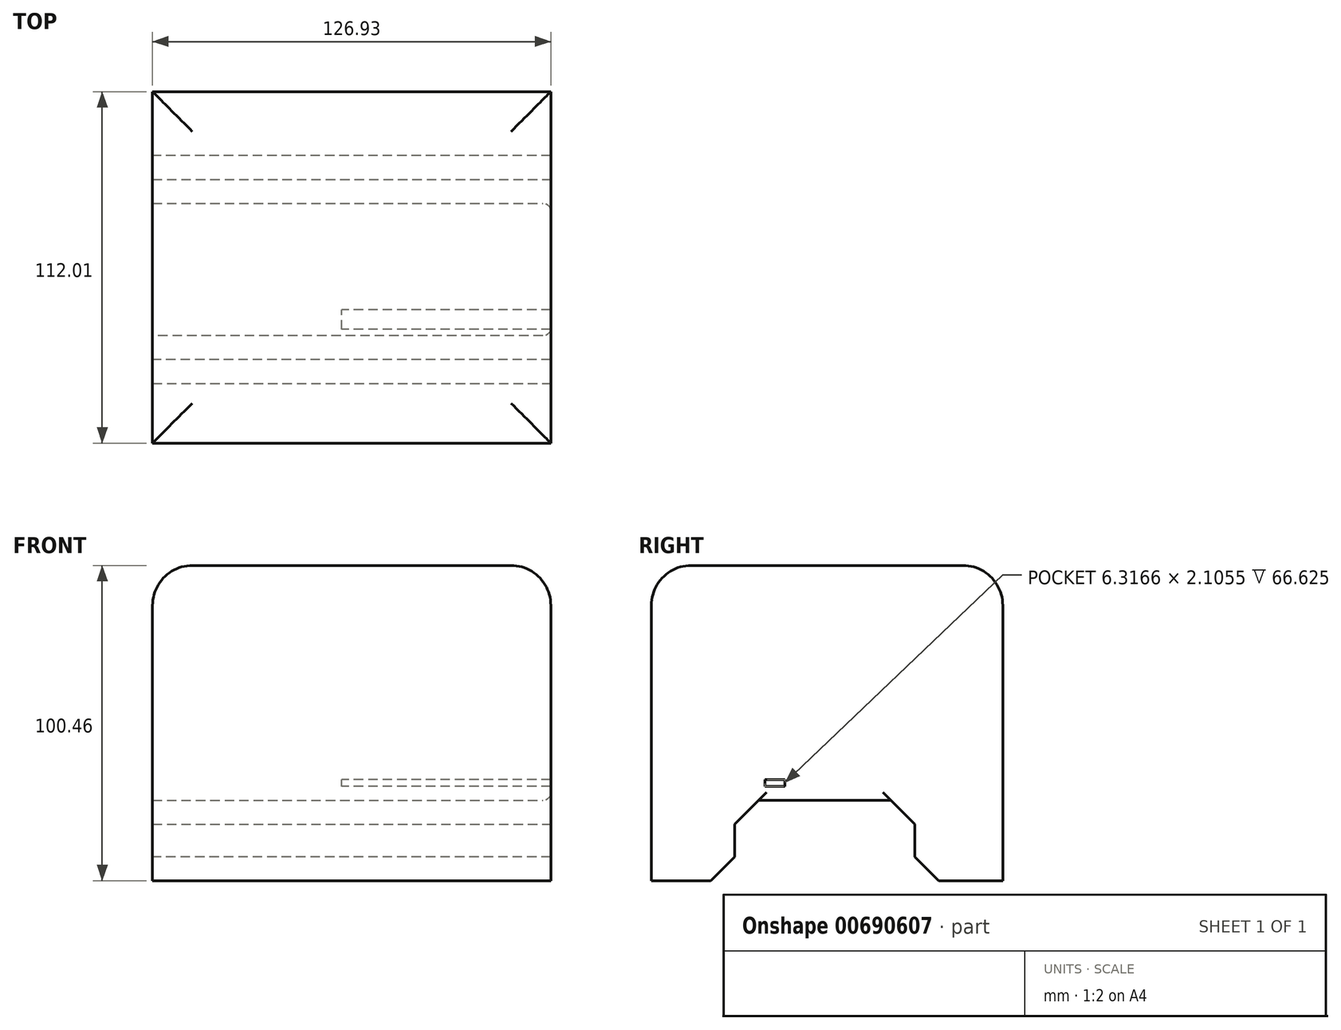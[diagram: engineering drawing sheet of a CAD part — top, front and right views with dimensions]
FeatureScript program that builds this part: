
annotation { "Feature Type Name" : "Feature", "Feature Type Description" : "" }
export const myFeature = defineFeature(function(context is Context, id is Id, definition is map)
    precondition{}
    {
        {
            var Q0;
            Q0=qCreatedBy(makeId("Front.planeOp"),FACE);
            var sketch = newSketch(context, id + "F0", { "sketchPlane" : qUnion([Q0])});
            skLineSegment(sketch, "E0.bottom", {"start": v(-60.3, 54) * mm, "end": v(66.62, 54) * mm});
            skLineSegment(sketch, "E0.top", {"start": v(-60.3, -46.47) * mm, "end": v(66.62, -46.47) * mm});
            skLineSegment(sketch, "E0.left", {"start": v(-60.3, 54) * mm, "end": v(-60.3, -46.47) * mm});
            skLineSegment(sketch, "E0.right", {"start": v(66.62, 54) * mm, "end": v(66.62, -46.47) * mm});
            skSolve(sketch);
        }
        {
            var Q0;
            Q0=makeQuery(id+"F0.imprint","IMPRINT",FACE,{"disambiguationData":[TD([[makeQuery(id+"F0.imprint","IMPRINT",EDGE,{"derivedFrom":sQuery(id+"F0.wireOp",EDGE,"E0.bottom")}),-1.0]])]});
            extrude(context, id + "F1", {"entities" : qUnion([Q0]), "depth" : 112.01 * mm, "offsetDistance" : 25.4 * mm});
        }
        {
            var Q0;
            Q0=makeQuery(id+"F1.opExtrude","CAP_EDGE",EDGE,{"disambiguationData":[OSD([sQuery(id+"F0.wireOp",EDGE,"E0.bottom")])],"isStart":false});
            var Q1;
            Q1=makeQuery(id+"F1.opExtrude","SWEPT_EDGE",EDGE,{"disambiguationData":[OSD([sQuery(id+"F0.wireOp",EDGE,"E0.bottom"),sQuery(id+"F0.wireOp",EDGE,"E0.right")])]});
            var Q2;
            Q2=makeQuery(id+"F1.opExtrude","CAP_EDGE",EDGE,{"disambiguationData":[OSD([sQuery(id+"F0.wireOp",EDGE,"E0.bottom")])],"isStart":true});
            var Q3;
            Q3=makeQuery(id+"F1.opExtrude","SWEPT_EDGE",EDGE,{"disambiguationData":[OSD([sQuery(id+"F0.wireOp",EDGE,"E0.bottom"),sQuery(id+"F0.wireOp",EDGE,"E0.left")])]});
            fillet(context, id + "F2", {"entities" : qUnion([Q0, Q1, Q2, Q3]), "radius" : 12.7 * mm, "tangentPropagation" : true, "allowEdgeOverflow" : false});
        }
        {
            var Q0;
            Q0=qCreatedBy(makeId("Right.planeOp"),FACE);
            var sketch = newSketch(context, id + "F3", { "sketchPlane" : qUnion([Q0])});
            skLineSegment(sketch, "E1.bottom", {"start": v(-85.43, -56.7) * mm, "end": v(-27.98, -56.7) * mm});
            skLineSegment(sketch, "E1.top", {"start": v(-85.43, -20.9) * mm, "end": v(-27.98, -20.9) * mm});
            skLineSegment(sketch, "E1.left", {"start": v(-85.43, -56.7) * mm, "end": v(-85.43, -20.9) * mm});
            skLineSegment(sketch, "E1.right", {"start": v(-27.98, -56.7) * mm, "end": v(-27.98, -20.9) * mm});
            skSolve(sketch);
        }
        {
            var Q0;
            Q0 = qSketchRegion(id + "F3", true);
            extrude(context, id + "F4", {"entities" : qUnion([Q0]), "depth" : 166.37 * mm, "offsetDistance" : 25.4 * mm});
        }
        {
            var Q0;
            Q0=makeQuery(id+"F4.opExtrude","CAP_FACE",FACE,{"disambiguationData":[OSD([sQuery(id+"F3.wireOp",EDGE,"E1.bottom"),sQuery(id+"F3.wireOp",EDGE,"E1.top"),sQuery(id+"F3.wireOp",EDGE,"E1.left"),sQuery(id+"F3.wireOp",EDGE,"E1.right")])],"isStart":false});
            extrude(context, id + "F5", {"entities" : qUnion([Q0]), "operationType" : NewBodyOperationType.ADD, "depth" : 99.82 * mm, "offsetDistance" : 25.4 * mm});
        }
        {
            var Q0;
            Q0=makeQuery(id+"F4.opExtrude","SWEPT_BODY",BODY,{"disambiguationData":[OSD([sQuery(id+"F3.wireOp",EDGE,"E1.bottom"),sQuery(id+"F3.wireOp",EDGE,"E1.top"),sQuery(id+"F3.wireOp",EDGE,"E1.left"),sQuery(id+"F3.wireOp",EDGE,"E1.right")])]});
            transform(context, id + "F6", {"entities" : qUnion([Q0]), "transformType" : TransformType.TRANSLATION_3D, "dx" : -151.38 * mm, "dy" : 0 * mm, "dz" : 0 * mm, "makeCopy" : false});
        }
        {
            var Q0;
            Q0=makeQuery(id+"F4.opExtrude","SWEPT_BODY",BODY,{"disambiguationData":[OSD([sQuery(id+"F3.wireOp",EDGE,"E1.bottom"),sQuery(id+"F3.wireOp",EDGE,"E1.top"),sQuery(id+"F3.wireOp",EDGE,"E1.left"),sQuery(id+"F3.wireOp",EDGE,"E1.right")])]});
            var Q1;
            Q1=makeQuery(id+"F1.opExtrude","SWEPT_BODY",BODY,{"disambiguationData":[OSD([sQuery(id+"F0.wireOp",EDGE,"E0.bottom"),sQuery(id+"F0.wireOp",EDGE,"E0.top"),sQuery(id+"F0.wireOp",EDGE,"E0.left"),sQuery(id+"F0.wireOp",EDGE,"E0.right")])]});
            booleanBodies(context, id + "F7", {"operationType" : BooleanOperationType.SUBTRACTION, "tools" : qUnion([Q0]), "targets" : qUnion([Q1])});
        }
        {
            var Q0;
            {var subQ0=sQuery(id+"F3.wireOp",EDGE,"E1.left");Q0=makeQuery(id+"F7.opBoolean","INTERSECT",EDGE,{"derivedFrom":[makeQuery(id+"F1.opExtrude","SWEPT_FACE",FACE,{"disambiguationData":[OSD([sQuery(id+"F0.wireOp",EDGE,"E0.top")])]}),makeQuery(id+"F5.boolean.opBoolean","MERGE",FACE,{"derivedFrom":[makeQuery(id+"F4.opExtrude","SWEPT_FACE",FACE,{"disambiguationData":[OSD([subQ0])]}),makeQuery(id+"F5.opExtrude","SWEPT_FACE",FACE,{"disambiguationData":[OSD([subQ0])]})]})]});}
            var Q1;
            {var subQ0=sQuery(id+"F3.wireOp",EDGE,"E1.right");Q1=makeQuery(id+"F7.opBoolean","INTERSECT",EDGE,{"derivedFrom":[makeQuery(id+"F1.opExtrude","SWEPT_FACE",FACE,{"disambiguationData":[OSD([sQuery(id+"F0.wireOp",EDGE,"E0.top")])]}),makeQuery(id+"F5.boolean.opBoolean","MERGE",FACE,{"derivedFrom":[makeQuery(id+"F4.opExtrude","SWEPT_FACE",FACE,{"disambiguationData":[OSD([subQ0])]}),makeQuery(id+"F5.opExtrude","SWEPT_FACE",FACE,{"disambiguationData":[OSD([subQ0])]})]})]});}
            var Q2;
            {var subQ0=sQuery(id+"F3.wireOp",EDGE,"E1.right");var subQ1=sQuery(id+"F3.wireOp",EDGE,"E1.top");Q2=makeQuery(id+"F7.opBoolean","COPY",EDGE,{"derivedFrom":makeQuery(id+"F5.boolean.opBoolean","MERGE",EDGE,{"derivedFrom":[makeQuery(id+"F4.opExtrude","SWEPT_EDGE",EDGE,{"disambiguationData":[OSD([subQ1,subQ0])]}),makeQuery(id+"F5.opExtrude","SWEPT_EDGE",EDGE,{"disambiguationData":[OSD([subQ1,subQ0])]})]})});}
            var Q3;
            {var subQ0=sQuery(id+"F3.wireOp",EDGE,"E1.left");var subQ1=sQuery(id+"F3.wireOp",EDGE,"E1.top");Q3=makeQuery(id+"F7.opBoolean","COPY",EDGE,{"derivedFrom":makeQuery(id+"F5.boolean.opBoolean","MERGE",EDGE,{"derivedFrom":[makeQuery(id+"F4.opExtrude","SWEPT_EDGE",EDGE,{"disambiguationData":[OSD([subQ1,subQ0])]}),makeQuery(id+"F5.opExtrude","SWEPT_EDGE",EDGE,{"disambiguationData":[OSD([subQ1,subQ0])]})]})});}
            chamfer(context, id + "F8", {"entities" : qUnion([Q0, Q1, Q2, Q3]), "width" : 7.62 * mm, "tangentPropagation" : true});
        }
        {
            var Q0;
            Q0=qCreatedBy(makeId("Right.planeOp"),FACE);
            var sketch = newSketch(context, id + "F9", { "sketchPlane" : qUnion([Q0])});
            skLineSegment(sketch, "E2.bottom", {"start": v(-75.8, -16.4) * mm, "end": v(-69.5, -16.4) * mm});
            skLineSegment(sketch, "E2.top", {"start": v(-75.8, -14.29) * mm, "end": v(-69.5, -14.29) * mm});
            skLineSegment(sketch, "E2.left", {"start": v(-75.8, -16.4) * mm, "end": v(-75.8, -14.29) * mm});
            skLineSegment(sketch, "E2.right", {"start": v(-69.5, -16.4) * mm, "end": v(-69.5, -14.29) * mm});
            skSolve(sketch);
        }
        {
            var Q0;
            Q0 = qSketchRegion(id + "F9", true);
            extrude(context, id + "F10", {"entities" : qUnion([Q0]), "operationType" : NewBodyOperationType.REMOVE, "depth" : 148.84 * mm, "offsetDistance" : 25.4 * mm});
        }
        {
            var Q0;
            {var subQ0=sQuery(id+"F3.wireOp",EDGE,"E1.top");Q0=makeQuery(id+"F7.opBoolean","INTERSECT",EDGE,{"derivedFrom":[makeQuery(id+"F1.opExtrude","SWEPT_FACE",FACE,{"disambiguationData":[OSD([sQuery(id+"F0.wireOp",EDGE,"E0.right")])]}),makeQuery(id+"F5.boolean.opBoolean","MERGE",FACE,{"derivedFrom":[makeQuery(id+"F4.opExtrude","SWEPT_FACE",FACE,{"disambiguationData":[OSD([subQ0])]}),makeQuery(id+"F5.opExtrude","SWEPT_FACE",FACE,{"disambiguationData":[OSD([subQ0])]})]})]});}
            fillet(context, id + "F11", {"entities" : qUnion([Q0]), "radius" : 2.54 * mm, "tangentPropagation" : true, "allowEdgeOverflow" : false});
        }
    });
